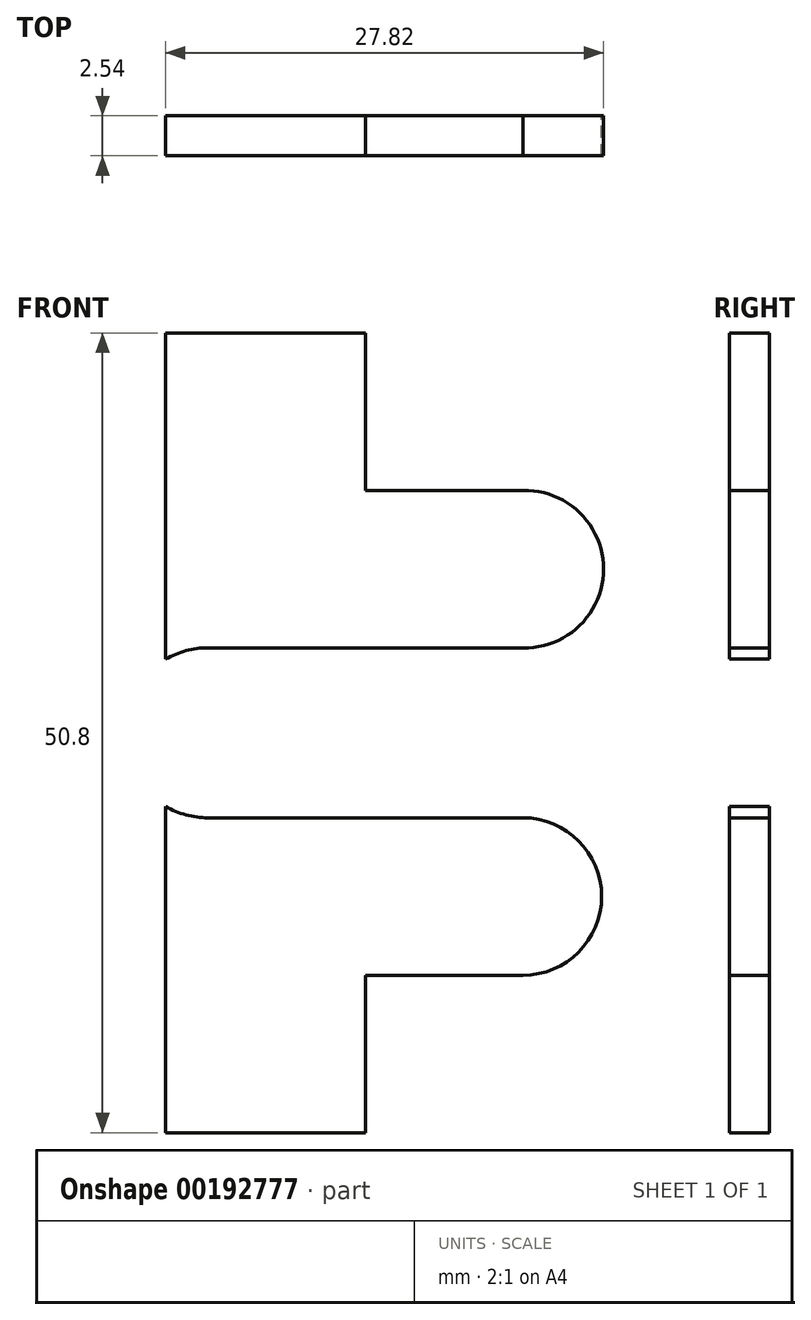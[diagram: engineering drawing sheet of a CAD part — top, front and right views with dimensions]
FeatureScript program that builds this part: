
annotation { "Feature Type Name" : "Feature", "Feature Type Description" : "" }
export const myFeature = defineFeature(function(context is Context, id is Id, definition is map)
    precondition{}
    {
        {
            var Q0;
            Q0=qCreatedBy(makeId("Front.planeOp"),FACE);
            var sketch = newSketch(context, id + "F0", { "sketchPlane" : qUnion([Q0])});
            skLineSegment(sketch, "E0.bottom", {"start": v(114.3, -50.8) * mm, "end": v(-114.3, -50.8) * mm});
            skLineSegment(sketch, "E0.top", {"start": v(114.3, 50.8) * mm, "end": v(-114.3, 50.8) * mm});
            skLineSegment(sketch, "E0.left", {"start": v(114.3, -50.8) * mm, "end": v(114.3, 50.8) * mm});
            skLineSegment(sketch, "E0.right", {"start": v(-114.3, -50.8) * mm, "end": v(-114.3, 50.8) * mm});
            skPoint(sketch, "E0.middle", {"position": v(0, 0) * mm});
            skLineSegment(sketch, "E1.bottom", {"start": v(114.3, 35.57) * mm, "end": v(127, 35.57) * mm});
            skLineSegment(sketch, "E1.top", {"start": v(114.3, -15.23) * mm, "end": v(127, -15.23) * mm});
            skLineSegment(sketch, "E1.left", {"start": v(127, 35.57) * mm, "end": v(127, -15.23) * mm});
            skLineSegment(sketch, "E1.right", {"start": v(114.3, 35.57) * mm, "end": v(114.3, -15.23) * mm});
            skPoint(sketch, "E2", {"position": v(127, -5.23) * mm});
            skPoint(sketch, "E3", {"position": v(127, 25.57) * mm});
            skPoint(sketch, "E4", {"position": v(127, 4.77) * mm});
            skPoint(sketch, "E5", {"position": v(127, 15.56) * mm});
            skLineSegment(sketch, "E6", {"start": v(127, -5.23) * mm, "end": v(137, -5.23) * mm});
            skLineSegment(sketch, "E7", {"start": v(127, 4.77) * mm, "end": v(137, 4.77) * mm});
            skLineSegment(sketch, "E8", {"start": v(127, 15.56) * mm, "end": v(137, 15.56) * mm});
            skLineSegment(sketch, "E9", {"start": v(127, 25.57) * mm, "end": v(137, 25.57) * mm});
            skCircle(sketch, "E10", {"center": v(137, -0.23) * mm, "radius": 5 * mm});
            skPoint(sketch, "E10.third.point", {"position": v(141.87, -1.35) * mm});
            skCircle(sketch, "E11", {"center": v(137.11, 20.57) * mm, "radius": 5 * mm});
            skPoint(sketch, "E11.third.point", {"position": v(142.01, 19.54) * mm});
            skLineSegment(sketch, "E12", {"start": v(127, 4.77) * mm, "end": v(117, 4.77) * mm});
            skLineSegment(sketch, "E13", {"start": v(127, 15.56) * mm, "end": v(117, 15.56) * mm});
            skCircle(sketch, "E14", {"center": v(117, 10.17) * mm, "radius": 5.4 * mm});
            skPoint(sketch, "E14.third.point", {"position": v(111.62, 9.68) * mm});
            skPoint(sketch, "E15", {"position": v(-114.3, -15.23) * mm});
            skPoint(sketch, "E16", {"position": v(-114.3, 35.57) * mm});
            skLineSegment(sketch, "E17.bottom", {"start": v(-109.22, -15.23) * mm, "end": v(-105.41, -15.23) * mm});
            skLineSegment(sketch, "E17.top", {"start": v(-109.22, 35.57) * mm, "end": v(-105.41, 35.57) * mm});
            skLineSegment(sketch, "E17.left", {"start": v(-109.22, -15.23) * mm, "end": v(-109.22, 35.57) * mm});
            skLineSegment(sketch, "E17.right", {"start": v(-105.41, -15.23) * mm, "end": v(-105.41, 35.57) * mm});
            skLineSegment(sketch, "E18.bottom", {"start": v(97.79, 38.1) * mm, "end": v(110.49, 38.1) * mm});
            skLineSegment(sketch, "E18.top", {"start": v(97.79, 35.56) * mm, "end": v(110.49, 35.56) * mm});
            skLineSegment(sketch, "E18.left", {"start": v(97.79, 38.1) * mm, "end": v(97.79, 35.56) * mm});
            skLineSegment(sketch, "E18.right", {"start": v(110.49, 38.1) * mm, "end": v(110.49, 35.56) * mm});
            skLineSegment(sketch, "E19.1.0.0", {"start": v(79.5, 38.1) * mm, "end": v(92.2, 38.1) * mm});
            skLineSegment(sketch, "E19.1.0.1", {"start": v(79.5, 35.56) * mm, "end": v(92.2, 35.56) * mm});
            skLineSegment(sketch, "E19.1.0.2", {"start": v(79.5, 38.1) * mm, "end": v(79.5, 35.56) * mm});
            skLineSegment(sketch, "E19.1.0.3", {"start": v(92.2, 38.1) * mm, "end": v(92.2, 35.56) * mm});
            skLineSegment(sketch, "E19.2.0.0", {"start": v(61.21, 38.1) * mm, "end": v(73.91, 38.1) * mm});
            skLineSegment(sketch, "E19.2.0.1", {"start": v(61.21, 35.56) * mm, "end": v(73.91, 35.56) * mm});
            skLineSegment(sketch, "E19.2.0.2", {"start": v(61.21, 38.1) * mm, "end": v(61.21, 35.56) * mm});
            skLineSegment(sketch, "E19.2.0.3", {"start": v(73.91, 38.1) * mm, "end": v(73.91, 35.56) * mm});
            skLineSegment(sketch, "E19.direction1", {"start": v(97.79, 35.56) * mm, "end": v(79.5, 35.56) * mm, "construction": true});
            skLineSegment(sketch, "E20.0.3.0", {"start": v(42.93, 38.1) * mm, "end": v(55.63, 38.1) * mm});
            skLineSegment(sketch, "E20.3.3.0", {"start": v(42.93, 35.56) * mm, "end": v(55.63, 35.56) * mm});
            skLineSegment(sketch, "E20.6.3.0", {"start": v(42.93, 38.1) * mm, "end": v(42.93, 35.56) * mm});
            skLineSegment(sketch, "E20.9.3.0", {"start": v(55.63, 38.1) * mm, "end": v(55.63, 35.56) * mm});
            skLineSegment(sketch, "E20.0.4.0", {"start": v(24.64, 38.1) * mm, "end": v(37.34, 38.1) * mm});
            skLineSegment(sketch, "E20.3.4.0", {"start": v(24.64, 35.56) * mm, "end": v(37.34, 35.56) * mm});
            skLineSegment(sketch, "E20.6.4.0", {"start": v(24.64, 38.1) * mm, "end": v(24.64, 35.56) * mm});
            skLineSegment(sketch, "E20.9.4.0", {"start": v(37.34, 38.1) * mm, "end": v(37.34, 35.56) * mm});
            skLineSegment(sketch, "E20.0.5.0", {"start": v(6.35, 38.1) * mm, "end": v(19.05, 38.1) * mm});
            skLineSegment(sketch, "E20.3.5.0", {"start": v(6.35, 35.56) * mm, "end": v(19.05, 35.56) * mm});
            skLineSegment(sketch, "E20.6.5.0", {"start": v(6.35, 38.1) * mm, "end": v(6.35, 35.56) * mm});
            skLineSegment(sketch, "E20.9.5.0", {"start": v(19.05, 38.1) * mm, "end": v(19.05, 35.56) * mm});
            skLineSegment(sketch, "E21.0.6.0", {"start": v(-11.94, 38.1) * mm, "end": v(0.76, 38.1) * mm});
            skLineSegment(sketch, "E21.3.6.0", {"start": v(-11.94, 35.56) * mm, "end": v(0.76, 35.56) * mm});
            skLineSegment(sketch, "E21.6.6.0", {"start": v(-11.94, 38.1) * mm, "end": v(-11.94, 35.56) * mm});
            skLineSegment(sketch, "E21.9.6.0", {"start": v(0.76, 38.1) * mm, "end": v(0.76, 35.56) * mm});
            skLineSegment(sketch, "E21.0.7.0", {"start": v(-30.23, 38.1) * mm, "end": v(-17.53, 38.1) * mm});
            skLineSegment(sketch, "E21.3.7.0", {"start": v(-30.23, 35.56) * mm, "end": v(-17.53, 35.56) * mm});
            skLineSegment(sketch, "E21.6.7.0", {"start": v(-30.23, 38.1) * mm, "end": v(-30.23, 35.56) * mm});
            skLineSegment(sketch, "E21.9.7.0", {"start": v(-17.53, 38.1) * mm, "end": v(-17.53, 35.56) * mm});
            skLineSegment(sketch, "E21.0.8.0", {"start": v(-48.51, 38.1) * mm, "end": v(-35.81, 38.1) * mm});
            skLineSegment(sketch, "E21.3.8.0", {"start": v(-48.51, 35.56) * mm, "end": v(-35.81, 35.56) * mm});
            skLineSegment(sketch, "E21.6.8.0", {"start": v(-48.51, 38.1) * mm, "end": v(-48.51, 35.56) * mm});
            skLineSegment(sketch, "E21.9.8.0", {"start": v(-35.81, 38.1) * mm, "end": v(-35.81, 35.56) * mm});
            skLineSegment(sketch, "E22.0.9.0", {"start": v(-66.8, 38.1) * mm, "end": v(-54.1, 38.1) * mm});
            skLineSegment(sketch, "E22.3.9.0", {"start": v(-66.8, 35.56) * mm, "end": v(-54.1, 35.56) * mm});
            skLineSegment(sketch, "E22.6.9.0", {"start": v(-66.8, 38.1) * mm, "end": v(-66.8, 35.56) * mm});
            skLineSegment(sketch, "E22.9.9.0", {"start": v(-54.1, 38.1) * mm, "end": v(-54.1, 35.56) * mm});
            skLineSegment(sketch, "E22.0.10.0", {"start": v(-85.09, 38.1) * mm, "end": v(-72.39, 38.1) * mm});
            skLineSegment(sketch, "E22.3.10.0", {"start": v(-85.09, 35.56) * mm, "end": v(-72.39, 35.56) * mm});
            skLineSegment(sketch, "E22.6.10.0", {"start": v(-85.09, 38.1) * mm, "end": v(-85.09, 35.56) * mm});
            skLineSegment(sketch, "E22.9.10.0", {"start": v(-72.39, 38.1) * mm, "end": v(-72.39, 35.56) * mm});
            skLineSegment(sketch, "E23.bottom", {"start": v(97.79, 33.02) * mm, "end": v(110.49, 33.02) * mm});
            skLineSegment(sketch, "E23.top", {"start": v(97.79, 30.48) * mm, "end": v(110.49, 30.48) * mm});
            skLineSegment(sketch, "E23.left", {"start": v(97.79, 33.02) * mm, "end": v(97.79, 30.48) * mm});
            skLineSegment(sketch, "E23.right", {"start": v(110.49, 33.02) * mm, "end": v(110.49, 30.48) * mm});
            skLineSegment(sketch, "E24.1.0.0", {"start": v(79.5, 33.02) * mm, "end": v(92.2, 33.02) * mm});
            skLineSegment(sketch, "E24.1.0.1", {"start": v(92.2, 33.02) * mm, "end": v(92.2, 30.48) * mm});
            skLineSegment(sketch, "E24.1.0.2", {"start": v(79.5, 30.48) * mm, "end": v(92.2, 30.48) * mm});
            skLineSegment(sketch, "E24.1.0.3", {"start": v(79.5, 33.02) * mm, "end": v(79.5, 30.48) * mm});
            skLineSegment(sketch, "E24.2.0.0", {"start": v(61.21, 33.02) * mm, "end": v(73.91, 33.02) * mm});
            skLineSegment(sketch, "E24.2.0.1", {"start": v(73.91, 33.02) * mm, "end": v(73.91, 30.48) * mm});
            skLineSegment(sketch, "E24.2.0.2", {"start": v(61.21, 30.48) * mm, "end": v(73.91, 30.48) * mm});
            skLineSegment(sketch, "E24.2.0.3", {"start": v(61.21, 33.02) * mm, "end": v(61.21, 30.48) * mm});
            skLineSegment(sketch, "E24.3.0.0", {"start": v(42.93, 33.02) * mm, "end": v(55.63, 33.02) * mm});
            skLineSegment(sketch, "E24.3.0.1", {"start": v(55.63, 33.02) * mm, "end": v(55.63, 30.48) * mm});
            skLineSegment(sketch, "E24.3.0.2", {"start": v(42.93, 30.48) * mm, "end": v(55.63, 30.48) * mm});
            skLineSegment(sketch, "E24.3.0.3", {"start": v(42.93, 33.02) * mm, "end": v(42.93, 30.48) * mm});
            skLineSegment(sketch, "E24.4.0.0", {"start": v(24.64, 33.02) * mm, "end": v(37.34, 33.02) * mm});
            skLineSegment(sketch, "E24.4.0.1", {"start": v(37.34, 33.02) * mm, "end": v(37.34, 30.48) * mm});
            skLineSegment(sketch, "E24.4.0.2", {"start": v(24.64, 30.48) * mm, "end": v(37.34, 30.48) * mm});
            skLineSegment(sketch, "E24.4.0.3", {"start": v(24.64, 33.02) * mm, "end": v(24.64, 30.48) * mm});
            skLineSegment(sketch, "E24.5.0.0", {"start": v(6.35, 33.02) * mm, "end": v(19.05, 33.02) * mm});
            skLineSegment(sketch, "E24.5.0.1", {"start": v(19.05, 33.02) * mm, "end": v(19.05, 30.48) * mm});
            skLineSegment(sketch, "E24.5.0.2", {"start": v(6.35, 30.48) * mm, "end": v(19.05, 30.48) * mm});
            skLineSegment(sketch, "E24.5.0.3", {"start": v(6.35, 33.02) * mm, "end": v(6.35, 30.48) * mm});
            skLineSegment(sketch, "E24.direction1", {"start": v(97.79, 33.02) * mm, "end": v(79.5, 33.02) * mm, "construction": true});
            skLineSegment(sketch, "E25.0.6.0", {"start": v(-11.94, 33.02) * mm, "end": v(0.76, 33.02) * mm});
            skLineSegment(sketch, "E25.3.6.0", {"start": v(0.76, 33.02) * mm, "end": v(0.76, 30.48) * mm});
            skLineSegment(sketch, "E25.6.6.0", {"start": v(-11.94, 30.48) * mm, "end": v(0.76, 30.48) * mm});
            skLineSegment(sketch, "E25.9.6.0", {"start": v(-11.94, 33.02) * mm, "end": v(-11.94, 30.48) * mm});
            skLineSegment(sketch, "E25.0.7.0", {"start": v(-30.23, 33.02) * mm, "end": v(-17.53, 33.02) * mm});
            skLineSegment(sketch, "E25.3.7.0", {"start": v(-17.53, 33.02) * mm, "end": v(-17.53, 30.48) * mm});
            skLineSegment(sketch, "E25.6.7.0", {"start": v(-30.23, 30.48) * mm, "end": v(-17.53, 30.48) * mm});
            skLineSegment(sketch, "E25.9.7.0", {"start": v(-30.23, 33.02) * mm, "end": v(-30.23, 30.48) * mm});
            skLineSegment(sketch, "E25.0.8.0", {"start": v(-48.51, 33.02) * mm, "end": v(-35.81, 33.02) * mm});
            skLineSegment(sketch, "E25.3.8.0", {"start": v(-35.81, 33.02) * mm, "end": v(-35.81, 30.48) * mm});
            skLineSegment(sketch, "E25.6.8.0", {"start": v(-48.51, 30.48) * mm, "end": v(-35.81, 30.48) * mm});
            skLineSegment(sketch, "E25.9.8.0", {"start": v(-48.51, 33.02) * mm, "end": v(-48.51, 30.48) * mm});
            skLineSegment(sketch, "E25.0.9.0", {"start": v(-66.8, 33.02) * mm, "end": v(-54.1, 33.02) * mm});
            skLineSegment(sketch, "E25.3.9.0", {"start": v(-54.1, 33.02) * mm, "end": v(-54.1, 30.48) * mm});
            skLineSegment(sketch, "E25.6.9.0", {"start": v(-66.8, 30.48) * mm, "end": v(-54.1, 30.48) * mm});
            skLineSegment(sketch, "E25.9.9.0", {"start": v(-66.8, 33.02) * mm, "end": v(-66.8, 30.48) * mm});
            skLineSegment(sketch, "E25.0.10.0", {"start": v(-85.1, 33.02) * mm, "end": v(-72.39, 33.02) * mm});
            skLineSegment(sketch, "E25.3.10.0", {"start": v(-72.39, 33.02) * mm, "end": v(-72.39, 30.48) * mm});
            skLineSegment(sketch, "E25.6.10.0", {"start": v(-85.1, 30.48) * mm, "end": v(-72.39, 30.48) * mm});
            skLineSegment(sketch, "E25.9.10.0", {"start": v(-85.1, 33.02) * mm, "end": v(-85.1, 30.48) * mm});
            skLineSegment(sketch, "E26.bottom", {"start": v(97.79, 27.94) * mm, "end": v(110.49, 27.94) * mm});
            skLineSegment(sketch, "E26.top", {"start": v(97.79, 25.4) * mm, "end": v(110.49, 25.4) * mm});
            skLineSegment(sketch, "E26.left", {"start": v(97.79, 27.94) * mm, "end": v(97.79, 25.4) * mm});
            skLineSegment(sketch, "E26.right", {"start": v(110.49, 27.94) * mm, "end": v(110.49, 25.4) * mm});
            skLineSegment(sketch, "E27.1.0.0", {"start": v(92.2, 27.94) * mm, "end": v(92.2, 25.4) * mm});
            skLineSegment(sketch, "E27.1.0.1", {"start": v(79.5, 27.94) * mm, "end": v(92.2, 27.94) * mm});
            skLineSegment(sketch, "E27.1.0.2", {"start": v(79.5, 25.4) * mm, "end": v(92.2, 25.4) * mm});
            skLineSegment(sketch, "E27.1.0.3", {"start": v(79.5, 27.94) * mm, "end": v(79.5, 25.4) * mm});
            skLineSegment(sketch, "E27.2.0.0", {"start": v(73.91, 27.94) * mm, "end": v(73.91, 25.4) * mm});
            skLineSegment(sketch, "E27.2.0.1", {"start": v(61.21, 27.94) * mm, "end": v(73.91, 27.94) * mm});
            skLineSegment(sketch, "E27.2.0.2", {"start": v(61.21, 25.4) * mm, "end": v(73.91, 25.4) * mm});
            skLineSegment(sketch, "E27.2.0.3", {"start": v(61.21, 27.94) * mm, "end": v(61.21, 25.4) * mm});
            skLineSegment(sketch, "E27.direction1", {"start": v(110.49, 25.4) * mm, "end": v(92.2, 25.4) * mm, "construction": true});
            skLineSegment(sketch, "E28.0.3.0", {"start": v(55.63, 27.94) * mm, "end": v(55.63, 25.4) * mm});
            skLineSegment(sketch, "E28.3.3.0", {"start": v(42.93, 27.94) * mm, "end": v(55.63, 27.94) * mm});
            skLineSegment(sketch, "E28.6.3.0", {"start": v(42.93, 25.4) * mm, "end": v(55.63, 25.4) * mm});
            skLineSegment(sketch, "E28.9.3.0", {"start": v(42.93, 27.94) * mm, "end": v(42.93, 25.4) * mm});
            skLineSegment(sketch, "E28.0.4.0", {"start": v(37.34, 27.94) * mm, "end": v(37.34, 25.4) * mm});
            skLineSegment(sketch, "E28.3.4.0", {"start": v(24.64, 27.94) * mm, "end": v(37.34, 27.94) * mm});
            skLineSegment(sketch, "E28.6.4.0", {"start": v(24.64, 25.4) * mm, "end": v(37.34, 25.4) * mm});
            skLineSegment(sketch, "E28.9.4.0", {"start": v(24.64, 27.94) * mm, "end": v(24.64, 25.4) * mm});
            skLineSegment(sketch, "E28.0.5.0", {"start": v(19.05, 27.94) * mm, "end": v(19.05, 25.4) * mm});
            skLineSegment(sketch, "E28.3.5.0", {"start": v(6.35, 27.94) * mm, "end": v(19.05, 27.94) * mm});
            skLineSegment(sketch, "E28.6.5.0", {"start": v(6.35, 25.4) * mm, "end": v(19.05, 25.4) * mm});
            skLineSegment(sketch, "E28.9.5.0", {"start": v(6.35, 27.94) * mm, "end": v(6.35, 25.4) * mm});
            skLineSegment(sketch, "E28.0.6.0", {"start": v(0.76, 27.94) * mm, "end": v(0.76, 25.4) * mm});
            skLineSegment(sketch, "E28.3.6.0", {"start": v(-11.94, 27.94) * mm, "end": v(0.76, 27.94) * mm});
            skLineSegment(sketch, "E28.6.6.0", {"start": v(-11.94, 25.4) * mm, "end": v(0.76, 25.4) * mm});
            skLineSegment(sketch, "E28.9.6.0", {"start": v(-11.94, 27.94) * mm, "end": v(-11.94, 25.4) * mm});
            skLineSegment(sketch, "E28.0.7.0", {"start": v(-17.53, 27.94) * mm, "end": v(-17.53, 25.4) * mm});
            skLineSegment(sketch, "E28.3.7.0", {"start": v(-30.23, 27.94) * mm, "end": v(-17.53, 27.94) * mm});
            skLineSegment(sketch, "E28.6.7.0", {"start": v(-30.23, 25.4) * mm, "end": v(-17.53, 25.4) * mm});
            skLineSegment(sketch, "E28.9.7.0", {"start": v(-30.23, 27.94) * mm, "end": v(-30.23, 25.4) * mm});
            skLineSegment(sketch, "E28.0.8.0", {"start": v(-35.81, 27.94) * mm, "end": v(-35.81, 25.4) * mm});
            skLineSegment(sketch, "E28.3.8.0", {"start": v(-48.51, 27.94) * mm, "end": v(-35.81, 27.94) * mm});
            skLineSegment(sketch, "E28.6.8.0", {"start": v(-48.51, 25.4) * mm, "end": v(-35.81, 25.4) * mm});
            skLineSegment(sketch, "E28.9.8.0", {"start": v(-48.51, 27.94) * mm, "end": v(-48.51, 25.4) * mm});
            skLineSegment(sketch, "E28.0.9.0", {"start": v(-54.1, 27.94) * mm, "end": v(-54.1, 25.4) * mm});
            skLineSegment(sketch, "E28.3.9.0", {"start": v(-66.8, 27.94) * mm, "end": v(-54.1, 27.94) * mm});
            skLineSegment(sketch, "E28.6.9.0", {"start": v(-66.8, 25.4) * mm, "end": v(-54.1, 25.4) * mm});
            skLineSegment(sketch, "E28.9.9.0", {"start": v(-66.8, 27.94) * mm, "end": v(-66.8, 25.4) * mm});
            skLineSegment(sketch, "E28.0.10.0", {"start": v(-72.39, 27.94) * mm, "end": v(-72.39, 25.4) * mm});
            skLineSegment(sketch, "E28.3.10.0", {"start": v(-85.09, 27.94) * mm, "end": v(-72.39, 27.94) * mm});
            skLineSegment(sketch, "E28.6.10.0", {"start": v(-85.09, 25.4) * mm, "end": v(-72.39, 25.4) * mm});
            skLineSegment(sketch, "E28.9.10.0", {"start": v(-85.09, 27.94) * mm, "end": v(-85.09, 25.4) * mm});
            skSolve(sketch);
        }
        {
            var Q0;
            {var subQ1=sQuery(id+"F0.wireOp",EDGE,"E1.top");Q0=makeQuery(id+"F0.imprint","IMPRINT",FACE,{"disambiguationData":[TD([[makeQuery(id+"F0.imprint","IMPRINT",EDGE,{"derivedFrom":subQ1}),1.0]])]});}
            var Q1;
            {var subQ1=sQuery(id+"F0.wireOp",EDGE,"E1.bottom");Q1=makeQuery(id+"F0.imprint","IMPRINT",FACE,{"disambiguationData":[TD([[makeQuery(id+"F0.imprint","IMPRINT",EDGE,{"derivedFrom":subQ1}),-1.0]])]});}
            var Q2;
            {var subQ0=sQuery(id+"F0.wireOp",EDGE,"E11");var subQ1=makeQuery(id+"F0.imprint","INTERSECT",VERTEX,{"derivedFrom":[sQuery(id+"F0.wireOp",EDGE,"E8"),subQ0]});Q2=makeQuery(id+"F0.imprint","IMPRINT",FACE,{"disambiguationData":[TD([[makeQuery(id+"F0.imprint","IMPRINT",EDGE,{"disambiguationData":[TD([[subQ1,1.0]])],"derivedFrom":subQ0}),1.0]])]});}
            var Q3;
            {var subQ0=sQuery(id+"F0.wireOp",EDGE,"E8");Q3=makeQuery(id+"F0.imprint","IMPRINT",FACE,{"disambiguationData":[TD([[makeQuery(id+"F0.imprint","IMPRINT",EDGE,{"derivedFrom":subQ0}),1.0]])]});}
            var Q4;
            {var subQ0=sQuery(id+"F0.wireOp",EDGE,"E10");var subQ1=makeQuery(id+"F0.imprint","INTERSECT",VERTEX,{"derivedFrom":[sQuery(id+"F0.wireOp",EDGE,"E6"),subQ0]});Q4=makeQuery(id+"F0.imprint","IMPRINT",FACE,{"disambiguationData":[TD([[makeQuery(id+"F0.imprint","IMPRINT",EDGE,{"disambiguationData":[TD([[subQ1,1.0]])],"derivedFrom":subQ0}),1.0]])]});}
            var Q5;
            {var subQ0=sQuery(id+"F0.wireOp",EDGE,"E6");Q5=makeQuery(id+"F0.imprint","IMPRINT",FACE,{"disambiguationData":[TD([[makeQuery(id+"F0.imprint","IMPRINT",EDGE,{"derivedFrom":subQ0}),1.0]])]});}
            extrude(context, id + "F1", {"entities" : qUnion([Q0, Q1, Q2, Q3, Q4, Q5]), "depth" : 2.54 * mm});
        }
    });
